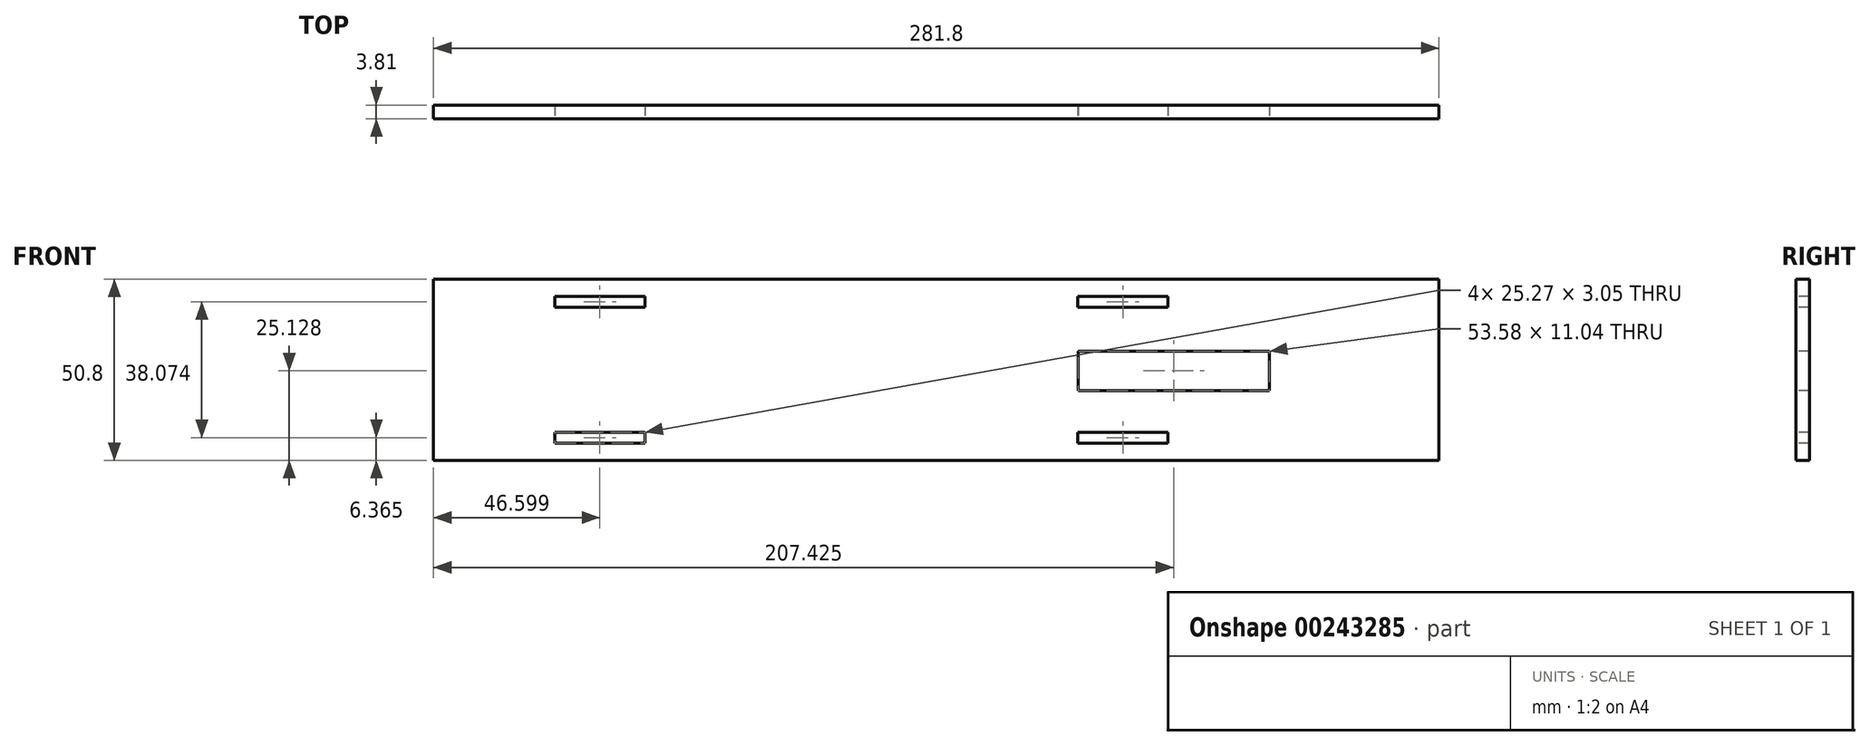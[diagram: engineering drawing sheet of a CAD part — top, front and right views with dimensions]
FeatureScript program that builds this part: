
annotation { "Feature Type Name" : "Feature", "Feature Type Description" : "" }
export const myFeature = defineFeature(function(context is Context, id is Id, definition is map)
    precondition{}
    {
        {
            var Q0;
            Q0=qCreatedBy(makeId("Front.planeOp"),FACE);
            var sketch = newSketch(context, id + "F0", { "sketchPlane" : qUnion([Q0])});
            skLineSegment(sketch, "E0.bottom", {"start": v(-122.7, 4.97) * mm, "end": v(159.09, 4.97) * mm});
            skLineSegment(sketch, "E0.top", {"start": v(-122.7, -45.83) * mm, "end": v(159.09, -45.83) * mm});
            skLineSegment(sketch, "E0.left", {"start": v(-122.7, 4.97) * mm, "end": v(-122.7, -45.83) * mm});
            skLineSegment(sketch, "E0.right", {"start": v(159.09, 4.97) * mm, "end": v(159.09, -45.83) * mm});
            skSolve(sketch);
        }
        {
            var Q0;
            Q0=makeQuery(id+"F0.imprint","IMPRINT",FACE,{"disambiguationData":[TD([[makeQuery(id+"F0.imprint","IMPRINT",EDGE,{"derivedFrom":sQuery(id+"F0.wireOp",EDGE,"E0.bottom")}),-1.0]])]});
            extrude(context, id + "F1", {"entities" : qUnion([Q0]), "depth" : 3.8 * mm});
        }
        {
            var Q0;
            Q0=makeQuery(id+"F1.opExtrude","CAP_FACE",FACE,{"disambiguationData":[OSD([sQuery(id+"F0.wireOp",EDGE,"E0.bottom"),sQuery(id+"F0.wireOp",EDGE,"E0.top"),sQuery(id+"F0.wireOp",EDGE,"E0.left"),sQuery(id+"F0.wireOp",EDGE,"E0.right")])],"isStart":false});
            var sketch = newSketch(context, id + "F2", { "sketchPlane" : qUnion([Q0])});
            skLineSegment(sketch, "E1", {"start": v(83.14, 0.13) * mm, "end": v(57.87, 0.13) * mm});
            skLineSegment(sketch, "E2", {"start": v(57.87, 0.13) * mm, "end": v(57.87, -2.91) * mm});
            skLineSegment(sketch, "E3", {"start": v(57.87, -2.91) * mm, "end": v(83.14, -2.91) * mm});
            skLineSegment(sketch, "E4", {"start": v(83.14, 0.13) * mm, "end": v(83.14, -2.91) * mm});
            skLineSegment(sketch, "E5", {"start": v(-122.7, -20.43) * mm, "end": v(159.09, -20.43) * mm});
            skLineSegment(sketch, "E6.MirrorCS", {"start": v(57.87, -37.94) * mm, "end": v(83.14, -37.94) * mm});
            skLineSegment(sketch, "E7.MirrorCS", {"start": v(83.14, -40.99) * mm, "end": v(57.87, -40.99) * mm});
            skLineSegment(sketch, "E8.MirrorCS", {"start": v(57.87, -40.99) * mm, "end": v(57.87, -37.94) * mm});
            skLineSegment(sketch, "E9.MirrorCS", {"start": v(83.14, -40.99) * mm, "end": v(83.14, -37.94) * mm});
            skLineSegment(sketch, "E10", {"start": v(-63.47, 0.13) * mm, "end": v(-88.75, 0.13) * mm});
            skLineSegment(sketch, "E11.bottom", {"start": v(-88.75, 0.13) * mm, "end": v(-63.47, 0.13) * mm});
            skLineSegment(sketch, "E11.top", {"start": v(-88.75, -2.91) * mm, "end": v(-63.47, -2.91) * mm});
            skLineSegment(sketch, "E11.left", {"start": v(-88.75, 0.13) * mm, "end": v(-88.75, -2.91) * mm});
            skLineSegment(sketch, "E11.right", {"start": v(-63.47, 0.13) * mm, "end": v(-63.47, -2.91) * mm});
            skLineSegment(sketch, "E12.MirrorCS", {"start": v(-88.75, -37.94) * mm, "end": v(-63.47, -37.94) * mm});
            skLineSegment(sketch, "E13.MirrorCS", {"start": v(-88.75, -40.99) * mm, "end": v(-88.75, -37.94) * mm});
            skLineSegment(sketch, "E14.MirrorCS", {"start": v(-88.75, -40.99) * mm, "end": v(-63.47, -40.99) * mm});
            skLineSegment(sketch, "E15.MirrorCS", {"start": v(-63.47, -40.99) * mm, "end": v(-63.47, -37.94) * mm});
            skSolve(sketch);
        }
        {
            var Q0;
            Q0 = qSketchRegion(id + "F2", true);
            extrude(context, id + "F3", {"entities" : qUnion([Q0]), "operationType" : NewBodyOperationType.REMOVE, "oppositeDirection" : true, "depth" : 25.4 * mm});
        }
        {
            var Q0;
            Q0=makeQuery(id+"F1.opExtrude","CAP_FACE",FACE,{"disambiguationData":[OSD([sQuery(id+"F0.wireOp",EDGE,"E0.bottom"),sQuery(id+"F0.wireOp",EDGE,"E0.top"),sQuery(id+"F0.wireOp",EDGE,"E0.left"),sQuery(id+"F0.wireOp",EDGE,"E0.right")])],"isStart":false});
            var sketch = newSketch(context, id + "F4", { "sketchPlane" : qUnion([Q0])});
            skLineSegment(sketch, "E16.bottom", {"start": v(67.16, -15.18) * mm, "end": v(111.5, -15.18) * mm});
            skLineSegment(sketch, "E17.MirrorCS", {"start": v(67.16, -26.22) * mm, "end": v(111.5, -26.22) * mm});
            skLineSegment(sketch, "E18.bottom", {"start": v(111.5, -15.18) * mm, "end": v(57.93, -15.18) * mm});
            skLineSegment(sketch, "E18.top", {"start": v(111.5, -26.22) * mm, "end": v(57.93, -26.22) * mm});
            skLineSegment(sketch, "E18.left", {"start": v(111.5, -15.18) * mm, "end": v(111.5, -26.22) * mm});
            skLineSegment(sketch, "E18.right", {"start": v(57.93, -15.18) * mm, "end": v(57.93, -26.22) * mm});
            skSolve(sketch);
        }
        {
            var Q0;
            {var subQ3=sQuery(id+"F4.wireOp",EDGE,"E18.left");Q0=makeQuery(id+"F4.imprint","IMPRINT",FACE,{"disambiguationData":[TD([[makeQuery(id+"F4.imprint","IMPRINT",EDGE,{"derivedFrom":subQ3}),-1.0]])]});}
            extrude(context, id + "F5", {"entities" : qUnion([Q0]), "operationType" : NewBodyOperationType.REMOVE, "oppositeDirection" : true, "depth" : 25.4 * mm});
        }
    });
